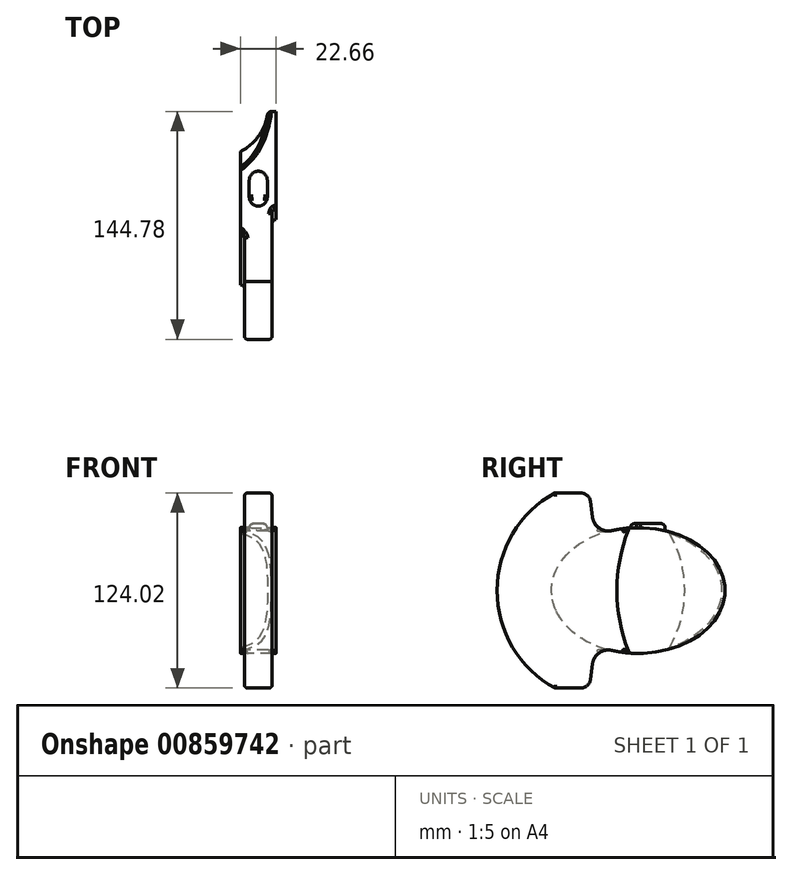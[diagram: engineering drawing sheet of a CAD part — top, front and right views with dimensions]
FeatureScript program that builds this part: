
annotation { "Feature Type Name" : "Feature", "Feature Type Description" : "" }
export const myFeature = defineFeature(function(context is Context, id is Id, definition is map)
    precondition{}
    {
        {
            var Q0;
            Q0=qCreatedBy(makeId("Right.planeOp"),FACE);
            var sketch = newSketch(context, id + "F0", { "sketchPlane" : qUnion([Q0])});
            skArc(sketch, "E0", {"start": v(-34, 62) * mm, "mid": v(-70.72, 0) * mm, "end": v(-34, -62) * mm});
            skLineSegment(sketch, "E1", {"start": v(0, 70.72) * mm, "end": v(0, -70.61) * mm, "construction": true});
            skLineSegment(sketch, "E2", {"start": v(70.61, 0) * mm, "end": v(-70.72, 0) * mm, "construction": true});
            skLineSegment(sketch, "E3", {"start": v(74.06, 0) * mm, "end": v(74.06, 57.76) * mm, "construction": true});
            skLineSegment(sketch, "E4", {"start": v(-34, 62) * mm, "end": v(-17.75, 62) * mm});
            skLineSegment(sketch, "E5.MirrorCS", {"start": v(-34, -62) * mm, "end": v(-17.75, -62) * mm});
            skArc(sketch, "E6", {"start": v(-11.36, 56.4) * mm, "mid": v(-13.5, 60.4) * mm, "end": v(-17.75, 62) * mm});
            skLineSegment(sketch, "E7", {"start": v(19.05, 0) * mm, "end": v(19.05, 39.94) * mm, "construction": true});
            skLineSegment(sketch, "E8", {"start": v(67.55, 39.94) * mm, "end": v(3.55, 39.94) * mm, "construction": true});
            skLineSegment(sketch, "E9.MirrorCS", {"start": v(67.55, -39.94) * mm, "end": v(3.55, -39.94) * mm, "construction": true});
            skEllipticalArc(sketch, "E10", {});
            skArc(sketch, "E11.MirrorC", {"start": v(-11.36, -56.4) * mm, "mid": v(-13.5, -60.4) * mm, "end": v(-17.75, -62) * mm});
            skArc(sketch, "E12", {"start": v(-10.07, 46.62) * mm, "mid": v(-5.79, 39.6) * mm, "end": v(2.3, 38.04) * mm});
            skLineSegment(sketch, "E13", {"start": v(-10.07, 46.62) * mm, "end": v(-11.36, 56.4) * mm});
            skLineSegment(sketch, "E14.MirrorCS", {"start": v(-10.07, -46.62) * mm, "end": v(-11.36, -56.4) * mm});
            skArc(sketch, "E15.MirrorCS", {"start": v(-10.07, -46.62) * mm, "mid": v(-5.79, -39.6) * mm, "end": v(2.3, -38.04) * mm});
            const initialGuessF0  = {"E10": [0.01905, 0, 1, 0, 0.055008018929324116, 0.039941500000000005, 4.402929078112277, 1.8802562290673104]};
            skSetInitialGuess(sketch, initialGuessF0);
            skSolve(sketch);
        }
        {
            var Q0;
            Q0 = qSketchRegion(id + "F0", true);
            extrude(context, id + "F1", {"entities" : qUnion([Q0]), "endBound" : BoundingType.SYMMETRIC, "depth" : 22.66 * mm, "offsetDistance" : 25 * mm});
        }
        {
            var Q0;
            Q0=makeQuery(id+"F1.opExtrude","CAP_FACE",FACE,{"disambiguationData":[OSD([sQuery(id+"F0.wireOp",EDGE,"E0"),sQuery(id+"F0.wireOp",EDGE,"E4"),sQuery(id+"F0.wireOp",EDGE,"E5.MirrorCS"),sQuery(id+"F0.wireOp",EDGE,"E6"),sQuery(id+"F0.wireOp",EDGE,"E10"),sQuery(id+"F0.wireOp",EDGE,"E11.MirrorC"),sQuery(id+"F0.wireOp",EDGE,"E12"),sQuery(id+"F0.wireOp",EDGE,"E13"),sQuery(id+"F0.wireOp",EDGE,"E14.MirrorCS"),sQuery(id+"F0.wireOp",EDGE,"E15.MirrorCS")])],"isStart":true});
            var sketch = newSketch(context, id + "F2", { "sketchPlane" : qUnion([Q0])});
            skCircle(sketch, "E16", {"center": v(23.21, 0) * mm, "radius": 71.86 * mm});
            skSolve(sketch);
        }
        {
            var Q0;
            Q0=qCreatedBy(makeId("Top.planeOp"),FACE);
            var sketch = newSketch(context, id + "F3", { "sketchPlane" : qUnion([Q0])});
            skLineSegment(sketch, "E17", {"start": v(6.13, 74.1) * mm, "end": v(-11.33, 74.1) * mm});
            skLineSegment(sketch, "E18", {"start": v(-11.33, 74.1) * mm, "end": v(-11.33, 48.58) * mm});
            skArc(sketch, "E19", {"start": v(-11.33, 48.58) * mm, "mid": v(0.71, 59.07) * mm, "end": v(6.13, 74.1) * mm});
            skSolve(sketch);
        }
        {
            var Q0;
            Q0 = qSketchRegion(id + "F3", true);
            var Q1;
            Q1 = qConstructionFilter(qBodyType(qCreatedBy(id + "F2" ,EDGE), BodyType.WIRE), ConstructionObject.NO);
            sweep(context, id + "F4", {"operationType" : NewBodyOperationType.REMOVE, "profiles" : qUnion([Q0]), "path" : qUnion([Q1])});
        }
        {
            var Q0;
            Q0=makeQuery(id+"F1.opExtrude","CAP_FACE",FACE,{"disambiguationData":[OSD([sQuery(id+"F0.wireOp",EDGE,"E0"),sQuery(id+"F0.wireOp",EDGE,"E4"),sQuery(id+"F0.wireOp",EDGE,"E5.MirrorCS"),sQuery(id+"F0.wireOp",EDGE,"E6"),sQuery(id+"F0.wireOp",EDGE,"E10"),sQuery(id+"F0.wireOp",EDGE,"E11.MirrorC"),sQuery(id+"F0.wireOp",EDGE,"E12"),sQuery(id+"F0.wireOp",EDGE,"E13"),sQuery(id+"F0.wireOp",EDGE,"E14.MirrorCS"),sQuery(id+"F0.wireOp",EDGE,"E15.MirrorCS")])],"isStart":true});
            var sketch = newSketch(context, id + "F5", { "sketchPlane" : qUnion([Q0])});
            skLineSegment(sketch, "E20", {"start": v(-19.5, 0) * mm, "end": v(-19.5, 39.94) * mm, "construction": true});
            skLineSegment(sketch, "E21", {"start": v(-19.5, 0) * mm, "end": v(-74.62, 0) * mm, "construction": true});
            skPoint(sketch, "E21.endSnap0", {"position": v(-48.58, 0) * mm});
            skLineSegment(sketch, "E22.MirrorCS", {"start": v(-19.5, 0) * mm, "end": v(-19.5, -39.94) * mm, "construction": true});
            skLineSegment(sketch, "E23.MirrorCS", {"start": v(-19.5, 0) * mm, "end": v(35.62, 0) * mm, "construction": true});
            skEllipse(sketch, "E24", {"center": v(-19.5, 0) * mm, "majorRadius": 55.12 * mm, "minorRadius": 39.94 * mm, "majorAxis": v(-1, 0)});
            skCircle(sketch, "E25", {"center": v(-112.15, 0) * mm, "radius": 106.68 * mm});
            skSolve(sketch);
        }
        {
            var Q0;
            Q0=qCreatedBy(makeId("Top.planeOp"),FACE);
            var sketch = newSketch(context, id + "F6", { "sketchPlane" : qUnion([Q0])});
            skLineSegment(sketch, "E26", {"start": v(-11.33, -83.31) * mm, "end": v(-8.8, -83.31) * mm});
            skLineSegment(sketch, "E27", {"start": v(-8.8, -83.31) * mm, "end": v(-8.8, -38.6) * mm});
            skArc(sketch, "E28", {"start": v(-8.8, -38.6) * mm, "mid": v(-9.54, -36.81) * mm, "end": v(-11.33, -36.07) * mm});
            skLineSegment(sketch, "E29", {"start": v(-11.33, -36.07) * mm, "end": v(-11.33, -83.31) * mm});
            skLineSegment(sketch, "E30", {"start": v(0, 0) * mm, "end": v(0, -77.7) * mm, "construction": true});
            skLineSegment(sketch, "E31.MirrorCS", {"start": v(11.33, 5.47) * mm, "end": v(11.33, -83.31) * mm});
            skLineSegment(sketch, "E32.MirrorCS", {"start": v(11.33, -83.31) * mm, "end": v(8.8, -83.31) * mm});
            skLineSegment(sketch, "E33", {"start": v(8.8, -83.31) * mm, "end": v(8.8, 2.93) * mm});
            skArc(sketch, "E34", {"start": v(11.33, 5.47) * mm, "mid": v(9.54, 4.73) * mm, "end": v(8.8, 2.93) * mm});
            skSolve(sketch);
        }
        {
            var Q0;
            Q0=makeQuery(id+"F6.imprint","IMPRINT",FACE,{"disambiguationData":[TD([[makeQuery(id+"F6.imprint","IMPRINT",EDGE,{"derivedFrom":sQuery(id+"F6.wireOp",EDGE,"E26")}),1.0]])]});
            var Q1;
            Q1=sQuery(id+"F5.wireOp",EDGE,"E24");
            sweep(context, id + "F7", {"operationType" : NewBodyOperationType.REMOVE, "profiles" : qUnion([Q0]), "path" : qUnion([Q1])});
        }
        {
            var Q0;
            Q0=makeQuery(id+"F6.imprint","IMPRINT",FACE,{"disambiguationData":[TD([[makeQuery(id+"F6.imprint","IMPRINT",EDGE,{"derivedFrom":sQuery(id+"F6.wireOp",EDGE,"E31.MirrorCS")}),-1.0]])]});
            var Q1;
            Q1=sQuery(id+"F5.wireOp",EDGE,"E25");
            sweep(context, id + "F8", {"operationType" : NewBodyOperationType.REMOVE, "profiles" : qUnion([Q0]), "path" : qUnion([Q1])});
        }
        {
            var Q0;
            Q0=qCreatedBy(makeId("Top.planeOp"),FACE);
            var sketch = newSketch(context, id + "F9", { "sketchPlane" : qUnion([Q0])});
            skArc(sketch, "E35", {"start": v(-5.72, 19.69) * mm, "mid": v(0, 13.97) * mm, "end": v(5.71, 19.69) * mm});
            skLineSegment(sketch, "E36", {"start": v(-5.71, 19.69) * mm, "end": v(-5.71, 30.35) * mm});
            skLineSegment(sketch, "E37", {"start": v(5.72, 30.35) * mm, "end": v(5.72, 19.69) * mm});
            skArc(sketch, "E38.trimOffspring", {"start": v(5.72, 30.35) * mm, "mid": v(0, 36.07) * mm, "end": v(-5.71, 30.35) * mm});
            skSolve(sketch);
        }
        {
            var Q0;
            Q0 = qSketchRegion(id + "F9", true);
            extrude(context, id + "F10", {"entities" : qUnion([Q0]), "operationType" : NewBodyOperationType.ADD, "depth" : 42.47 * mm, "offsetDistance" : 25 * mm});
        }
        {
            var Q0;
            Q0=makeQuery(id+"F7.boolean.opBoolean","INTERSECT",EDGE,{"derivedFrom":[makeQuery(id+"F1.opExtrude","SWEPT_FACE",FACE,{"disambiguationData":[OSD([sQuery(id+"F0.wireOp",EDGE,"E12")])]}),makeQuery(id+"F7.opSweep","SWEPT_FACE",FACE,{"disambiguationData":[OSD([sQuery(id+"F5.wireOp",EDGE,"E24"),sQuery(id+"F6.wireOp",EDGE,"E28")])]})]});
            var Q1;
            Q1=makeQuery(id+"F8.boolean.opBoolean","INTERSECT",EDGE,{"derivedFrom":[makeQuery(id+"F1.opExtrude","SWEPT_FACE",FACE,{"disambiguationData":[OSD([sQuery(id+"F0.wireOp",EDGE,"E12")])]}),makeQuery(id+"F8.opSweep","SWEPT_FACE",FACE,{"disambiguationData":[OSD([sQuery(id+"F5.wireOp",EDGE,"E25"),sQuery(id+"F6.wireOp",EDGE,"E33")])]})]});
            var Q2;
            Q2=makeQuery(id+"F8.boolean.opBoolean","INTERSECT",EDGE,{"derivedFrom":[makeQuery(id+"F1.opExtrude","SWEPT_FACE",FACE,{"disambiguationData":[OSD([sQuery(id+"F0.wireOp",EDGE,"E0")])]}),makeQuery(id+"F8.opSweep","SWEPT_FACE",FACE,{"disambiguationData":[OSD([sQuery(id+"F5.wireOp",EDGE,"E25"),sQuery(id+"F6.wireOp",EDGE,"E33")])]})]});
            var Q3;
            Q3=makeQuery(id+"F7.boolean.opBoolean","INTERSECT",EDGE,{"derivedFrom":[makeQuery(id+"F1.opExtrude","SWEPT_FACE",FACE,{"disambiguationData":[OSD([sQuery(id+"F0.wireOp",EDGE,"E0")])]}),makeQuery(id+"F7.opSweep","SWEPT_FACE",FACE,{"disambiguationData":[OSD([sQuery(id+"F5.wireOp",EDGE,"E24"),sQuery(id+"F6.wireOp",EDGE,"E27")])]})]});
            var Q4;
            Q4=makeQuery(id+"F8.boolean.opBoolean","INTERSECT",EDGE,{"derivedFrom":[makeQuery(id+"F1.opExtrude","SWEPT_FACE",FACE,{"disambiguationData":[OSD([sQuery(id+"F0.wireOp",EDGE,"E15.MirrorCS")])]}),makeQuery(id+"F8.opSweep","SWEPT_FACE",FACE,{"disambiguationData":[OSD([sQuery(id+"F5.wireOp",EDGE,"E25"),sQuery(id+"F6.wireOp",EDGE,"E33")])]})]});
            var Q5;
            Q5=makeQuery(id+"F7.boolean.opBoolean","INTERSECT",EDGE,{"derivedFrom":[makeQuery(id+"F1.opExtrude","SWEPT_FACE",FACE,{"disambiguationData":[OSD([sQuery(id+"F0.wireOp",EDGE,"E5.MirrorCS")])]}),makeQuery(id+"F7.opSweep","SWEPT_FACE",FACE,{"disambiguationData":[OSD([sQuery(id+"F5.wireOp",EDGE,"E24"),sQuery(id+"F6.wireOp",EDGE,"E27")])]})]});
            fillet(context, id + "F11", {"entities" : qUnion([Q0, Q1, Q2, Q3, Q4, Q5]), "radius" : 2.16 * mm, "tangentPropagation" : true, "allowEdgeOverflow" : false});
        }
        {
            var Q0;
            Q0=makeQuery(id+"F4.boolean.opBoolean","INTERSECT",EDGE,{"derivedFrom":[makeQuery(id+"F1.opExtrude","SWEPT_FACE",FACE,{"disambiguationData":[OSD([sQuery(id+"F0.wireOp",EDGE,"E10")])]}),makeQuery(id+"F4.opSweep","SWEPT_FACE",FACE,{"disambiguationData":[OSD([sQuery(id+"F2.wireOp",EDGE,"E16"),sQuery(id+"F3.wireOp",EDGE,"E19")])]})]});
            fillet(context, id + "F12", {"entities" : qUnion([Q0]), "radius" : 2.54 * mm, "tangentPropagation" : true, "allowEdgeOverflow" : false});
        }
        {
            var Q0;
            Q0=makeQuery(id+"F10.opExtrude","CAP_EDGE",EDGE,{"disambiguationData":[OSD([sQuery(id+"F9.wireOp",EDGE,"E35")])],"isStart":false});
            fillet(context, id + "F13", {"entities" : qUnion([Q0]), "radius" : 2.54 * mm, "tangentPropagation" : true, "allowEdgeOverflow" : false});
        }
    });
